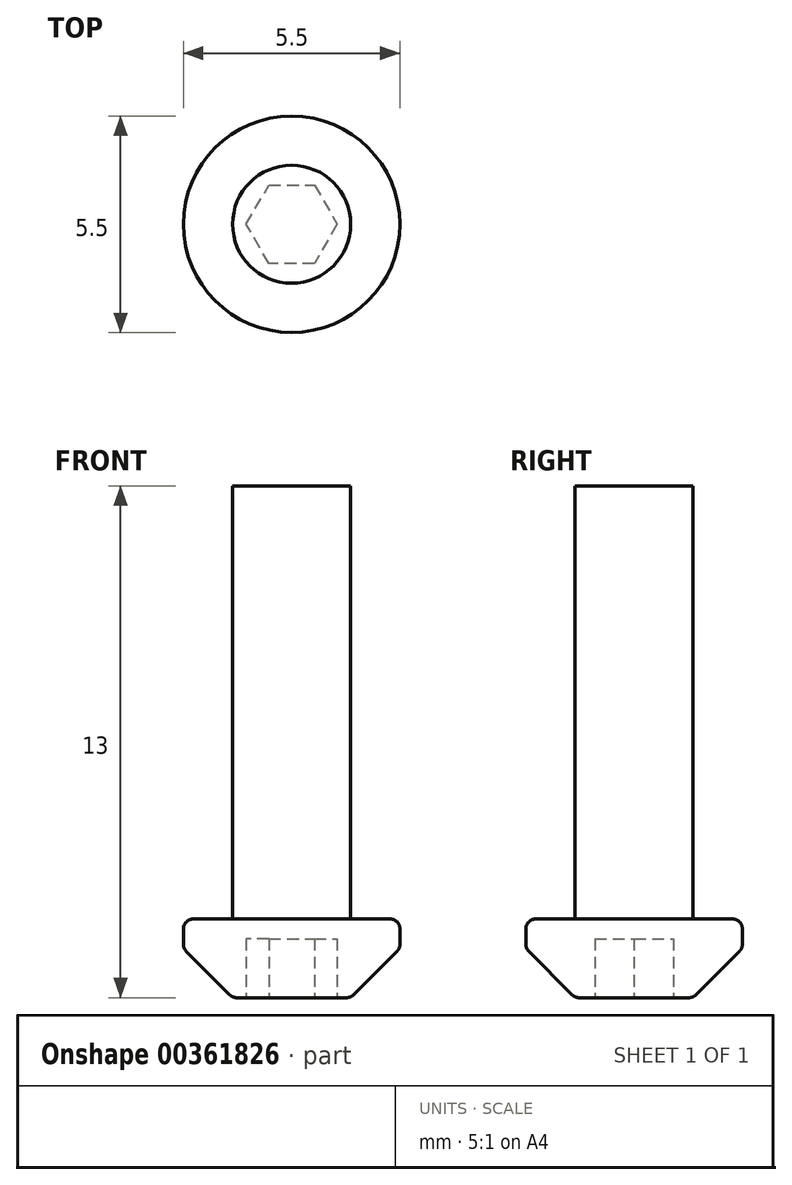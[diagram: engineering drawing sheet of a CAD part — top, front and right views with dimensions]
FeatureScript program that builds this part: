
annotation { "Feature Type Name" : "Feature", "Feature Type Description" : "" }
export const myFeature = defineFeature(function(context is Context, id is Id, definition is map)
    precondition{}
    {
        {
            assignVariable(context, id + "F0", {"name" : "ShaftLength", "anyValue" : 10});
        }
        {
            var Q0;
            Q0=qCreatedBy(makeId("Top.planeOp"),FACE);
            var sketch = newSketch(context, id + "F1", { "sketchPlane" : qUnion([Q0])});
            skCircle(sketch, "E0", {"center": v(0, 0) * mm, "radius": 2.75 * mm});
            skCircle(sketch, "E1.cCircle", {"center": v(0, 0) * mm, "radius": 1 * mm, "construction": true});
            skLineSegment(sketch, "E1.0", {"start": v(-1.15, 0) * mm, "end": v(-0.58, 1) * mm});
            skLineSegment(sketch, "E1.1", {"start": v(-0.58, 1) * mm, "end": v(0.58, 1) * mm});
            skLineSegment(sketch, "E1.2", {"start": v(0.58, 1) * mm, "end": v(1.15, 0) * mm});
            skLineSegment(sketch, "E1.3", {"start": v(1.15, 0) * mm, "end": v(0.58, -1) * mm});
            skLineSegment(sketch, "E1.4", {"start": v(0.58, -1) * mm, "end": v(-0.58, -1) * mm});
            skLineSegment(sketch, "E1.5", {"start": v(-0.58, -1) * mm, "end": v(-1.15, 0) * mm});
            skPoint(sketch, "E1.0.midPoint", {"position": v(-0.87, 0.5) * mm});
            skCircle(sketch, "E2", {"center": v(0, 0) * mm, "radius": 1.5 * mm});
            skSolve(sketch);
        }
        {
            var Q0;
            Q0=makeQuery(id+"F1.imprint","IMPRINT",FACE,{"disambiguationData":[TD([[makeQuery(id+"F1.imprint","IMPRINT",EDGE,{"derivedFrom":sQuery(id+"F1.wireOp",EDGE,"E0")}),1.0]])]});
            var Q1;
            Q1=makeQuery(id+"F1.imprint","IMPRINT",FACE,{"disambiguationData":[TD([[makeQuery(id+"F1.imprint","IMPRINT",EDGE,{"derivedFrom":sQuery(id+"F1.wireOp",EDGE,"E1.0")}),1.0]])]});
            extrude(context, id + "F2", {"entities" : qUnion([Q0, Q1]), "depth" : 2 * mm, "offsetDistance" : 25 * mm});
        }
        {
            var Q0;
            {var subQ0=sQuery(id+"F1.wireOp",EDGE,"E1.5");var subQ1=sQuery(id+"F1.wireOp",EDGE,"E1.4");var subQ2=makeQuery(id+"F1.imprint","INTERSECT",VERTEX,{"derivedFrom":[subQ1,subQ0]});Q0=makeQuery(id+"F1.imprint","IMPRINT",FACE,{"disambiguationData":[TD([[makeQuery(id+"F1.imprint","IMPRINT",EDGE,{"disambiguationData":[TD([[subQ2,1.0]])],"derivedFrom":subQ1}),-1.0]])]});}
            var Q1;
            {var subQ0=sQuery(id+"F1.wireOp",EDGE,"E1.4");var subQ1=sQuery(id+"F1.wireOp",EDGE,"E1.3");var subQ2=makeQuery(id+"F1.imprint","INTERSECT",VERTEX,{"derivedFrom":[subQ1,subQ0]});Q1=makeQuery(id+"F1.imprint","IMPRINT",FACE,{"disambiguationData":[TD([[makeQuery(id+"F1.imprint","IMPRINT",EDGE,{"disambiguationData":[TD([[subQ2,1.0]])],"derivedFrom":subQ1}),-1.0]])]});}
            var Q2;
            {var subQ0=sQuery(id+"F1.wireOp",EDGE,"E1.5");var subQ1=sQuery(id+"F1.wireOp",EDGE,"E1.0");var subQ2=makeQuery(id+"F1.imprint","INTERSECT",VERTEX,{"derivedFrom":[subQ1,subQ0]});Q2=makeQuery(id+"F1.imprint","IMPRINT",FACE,{"disambiguationData":[TD([[makeQuery(id+"F1.imprint","IMPRINT",EDGE,{"disambiguationData":[TD([[subQ2,-1.0]])],"derivedFrom":subQ1}),-1.0]])]});}
            var Q3;
            {var subQ0=sQuery(id+"F1.wireOp",EDGE,"E2");var subQ4=makeQuery(id+"F1.imprint","INTERSECT",VERTEX,{"derivedFrom":[sQuery(id+"F1.wireOp",EDGE,"E1.1"),subQ0]});Q3=makeQuery(id+"F1.imprint","IMPRINT",FACE,{"disambiguationData":[TD([[makeQuery(id+"F1.imprint","IMPRINT",EDGE,{"disambiguationData":[TD([[subQ4,1.0]])],"derivedFrom":subQ0}),1.0]])]});}
            var Q4;
            {var subQ0=sQuery(id+"F1.wireOp",EDGE,"E1.1");var subQ1=sQuery(id+"F1.wireOp",EDGE,"E1.0");var subQ2=makeQuery(id+"F1.imprint","INTERSECT",VERTEX,{"derivedFrom":[subQ1,subQ0]});Q4=makeQuery(id+"F1.imprint","IMPRINT",FACE,{"disambiguationData":[TD([[makeQuery(id+"F1.imprint","IMPRINT",EDGE,{"disambiguationData":[TD([[subQ2,1.0]])],"derivedFrom":subQ1}),-1.0]])]});}
            var Q5;
            {var subQ0=sQuery(id+"F1.wireOp",EDGE,"E1.2");var subQ1=sQuery(id+"F1.wireOp",EDGE,"E1.1");var subQ2=makeQuery(id+"F1.imprint","INTERSECT",VERTEX,{"derivedFrom":[subQ1,subQ0]});Q5=makeQuery(id+"F1.imprint","IMPRINT",FACE,{"disambiguationData":[TD([[makeQuery(id+"F1.imprint","IMPRINT",EDGE,{"disambiguationData":[TD([[subQ2,1.0]])],"derivedFrom":subQ1}),-1.0]])]});}
            var Q6;
            {var subQ0=sQuery(id+"F1.wireOp",EDGE,"E1.3");var subQ1=sQuery(id+"F1.wireOp",EDGE,"E1.2");var subQ2=makeQuery(id+"F1.imprint","INTERSECT",VERTEX,{"derivedFrom":[subQ1,subQ0]});Q6=makeQuery(id+"F1.imprint","IMPRINT",FACE,{"disambiguationData":[TD([[makeQuery(id+"F1.imprint","IMPRINT",EDGE,{"disambiguationData":[TD([[subQ2,1.0]])],"derivedFrom":subQ1}),-1.0]])]});}
            extrude(context, id + "F3", {"entities" : qUnion([Q0, Q1, Q2, Q3, Q4, Q5, Q6]), "operationType" : NewBodyOperationType.ADD, "depth" : 2 * mm, "offsetDistance" : 25 * mm, "hasSecondDirection" : true, "secondDirectionOppositeDirection" : false, "secondDirectionDepth" : 1.5 * mm});
        }
        {
            var Q0;
            {var subQ0=sQuery(id+"F1.wireOp",EDGE,"E2");var subQ4=makeQuery(id+"F1.imprint","INTERSECT",VERTEX,{"derivedFrom":[sQuery(id+"F1.wireOp",EDGE,"E1.1"),subQ0]});Q0=makeQuery(id+"F1.imprint","IMPRINT",FACE,{"disambiguationData":[TD([[makeQuery(id+"F1.imprint","IMPRINT",EDGE,{"disambiguationData":[TD([[subQ4,1.0]])],"derivedFrom":subQ0}),1.0]])]});}
            var Q1;
            Q1=makeQuery(id+"F1.imprint","IMPRINT",FACE,{"disambiguationData":[TD([[makeQuery(id+"F1.imprint","IMPRINT",EDGE,{"derivedFrom":sQuery(id+"F1.wireOp",EDGE,"E1.0")}),-1.0]])]});
            extrude(context, id + "F4", {"entities" : qUnion([Q0, Q1]), "operationType" : NewBodyOperationType.ADD, "depth" : (getVariable(context, 'ShaftLength') + 3) * mm, "offsetDistance" : 25 * mm, "hasSecondDirection" : true, "secondDirectionOppositeDirection" : false, "secondDirectionDepth" : 2 * mm});
        }
        {
            var Q0;
            Q0=makeQuery(id+"F2.opExtrude","CAP_EDGE",EDGE,{"disambiguationData":[OSD([sQuery(id+"F1.wireOp",EDGE,"E0")])],"isStart":true});
            chamfer(context, id + "F5", {"entities" : qUnion([Q0]), "chamferType" : ChamferType.TWO_OFFSETS, "width1" : 1.25 * mm, "oppositeDirection" : false, "width2" : 1.25 * mm, "tangentPropagation" : true});
        }
        {
            var Q0;
            Q0=makeQuery(id+"F2.opExtrude","CAP_EDGE",EDGE,{"disambiguationData":[OSD([sQuery(id+"F1.wireOp",EDGE,"E0")])],"isStart":false});
            var Q1;
            Q1=makeQuery(id+"F4.opExtrude","CAP_EDGE",EDGE,{"disambiguationData":[OSD([sQuery(id+"F1.wireOp",EDGE,"E2")])],"isStart":true});
            var Q2;
            {var subQ0=sQuery(id+"F1.wireOp",EDGE,"E0");Q2=makeQuery(id+"F5.opChamfer","BLEND_EDGE",EDGE,{"blendedFrom":[makeQuery(id+"F2.opExtrude","CAP_EDGE",EDGE,{"disambiguationData":[OSD([subQ0])],"isStart":true}),makeQuery(id+"F2.opExtrude","CAP_FACE",FACE,{"disambiguationData":[OSD([subQ0,sQuery(id+"F1.wireOp",EDGE,"E1.0"),sQuery(id+"F1.wireOp",EDGE,"E1.1"),sQuery(id+"F1.wireOp",EDGE,"E1.2"),sQuery(id+"F1.wireOp",EDGE,"E1.3"),sQuery(id+"F1.wireOp",EDGE,"E1.4"),sQuery(id+"F1.wireOp",EDGE,"E1.5")])],"isStart":true})],"blendedInto":[makeQuery(id+"F2.opExtrude","CAP_FACE",FACE,{"disambiguationData":[OSD([subQ0,sQuery(id+"F1.wireOp",EDGE,"E1.0"),sQuery(id+"F1.wireOp",EDGE,"E1.1"),sQuery(id+"F1.wireOp",EDGE,"E1.2"),sQuery(id+"F1.wireOp",EDGE,"E1.3"),sQuery(id+"F1.wireOp",EDGE,"E1.4"),sQuery(id+"F1.wireOp",EDGE,"E1.5")])],"isStart":true})]});}
            var Q3;
            {var subQ0=sQuery(id+"F1.wireOp",EDGE,"E0");Q3=makeQuery(id+"F5.opChamfer","BLEND_EDGE",EDGE,{"blendedFrom":[makeQuery(id+"F2.opExtrude","CAP_EDGE",EDGE,{"disambiguationData":[OSD([subQ0])],"isStart":true}),makeQuery(id+"F2.opExtrude","SWEPT_FACE",FACE,{"disambiguationData":[OSD([subQ0])]})],"blendedInto":[makeQuery(id+"F2.opExtrude","SWEPT_FACE",FACE,{"disambiguationData":[OSD([subQ0])]})]});}
            fillet(context, id + "F6", {"entities" : qUnion([Q0, Q1, Q2, Q3]), "radius" : .25 * mm, "tangentPropagation" : true, "allowEdgeOverflow" : false});
        }
    });
